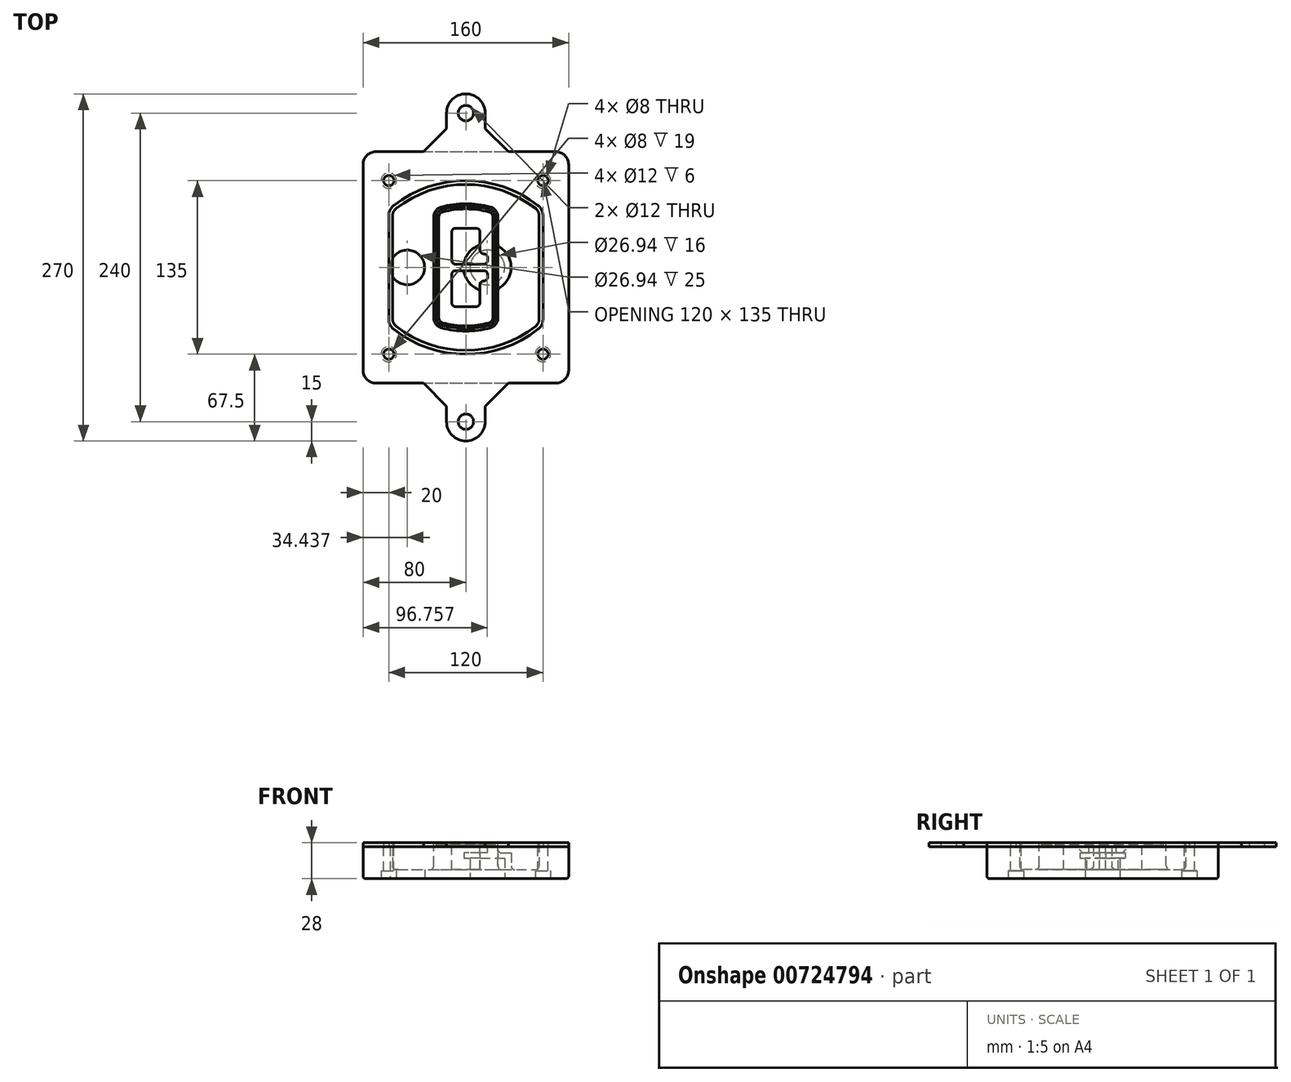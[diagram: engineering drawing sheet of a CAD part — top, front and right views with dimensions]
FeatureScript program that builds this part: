
annotation { "Feature Type Name" : "Feature", "Feature Type Description" : "" }
export const myFeature = defineFeature(function(context is Context, id is Id, definition is map)
    precondition{}
    {
        {
            var Q0;
            Q0=qCreatedBy(makeId("Top.planeOp"),FACE);
            var sketch = newSketch(context, id + "F0", { "sketchPlane" : qUnion([Q0])});
            skPoint(sketch, "E0.rect.middle", {"position": v(0, 0) * mm});
            skLineSegment(sketch, "E1.bottom", {"start": v(-70, -90) * mm, "end": v(70, -90) * mm});
            skLineSegment(sketch, "E1.top", {"start": v(-70, 90) * mm, "end": v(70, 90) * mm});
            skLineSegment(sketch, "E1.left", {"start": v(-80, -80) * mm, "end": v(-80, 80) * mm});
            skLineSegment(sketch, "E1.right", {"start": v(80, -80) * mm, "end": v(80, 80) * mm});
            skLineSegment(sketch, "E2", {"start": v(-80, 90) * mm, "end": v(80, -90) * mm, "construction": true});
            skLineSegment(sketch, "E3", {"start": v(80, 90) * mm, "end": v(-80, -90) * mm, "construction": true});
            skCircle(sketch, "E4", {"center": v(-60, 67.5) * mm, "radius": 4 * mm});
            skCircle(sketch, "E5", {"center": v(60, 67.5) * mm, "radius": 4 * mm});
            skCircle(sketch, "E6", {"center": v(60, -67.5) * mm, "radius": 4 * mm});
            skCircle(sketch, "E7", {"center": v(-60, -67.5) * mm, "radius": 4 * mm});
            skLineSegment(sketch, "E8", {"start": v(-60, 67.5) * mm, "end": v(60, 67.5) * mm, "construction": true});
            skLineSegment(sketch, "E9", {"start": v(60, 67.5) * mm, "end": v(60, -67.5) * mm, "construction": true});
            skLineSegment(sketch, "E10", {"start": v(60, -67.5) * mm, "end": v(-60, -67.5) * mm, "construction": true});
            skLineSegment(sketch, "E11", {"start": v(-60, -67.5) * mm, "end": v(-60, 67.5) * mm, "construction": true});
            skLineSegment(sketch, "E12", {"start": v(-60, 40.3) * mm, "end": v(-60, -40.3) * mm});
            skLineSegment(sketch, "E13", {"start": v(60, 40.3) * mm, "end": v(60, -40.3) * mm});
            skArc(sketch, "E14", {"start": v(56.15, 48.18) * mm, "mid": v(0, 67.5) * mm, "end": v(-56.15, 48.18) * mm});
            skArc(sketch, "E15", {"start": v(-56.15, -48.18) * mm, "mid": v(0, -67.5) * mm, "end": v(56.15, -48.18) * mm});
            skLineSegment(sketch, "E16", {"start": v(-60, 0) * mm, "end": v(60, 0) * mm, "construction": true});
            skPoint(sketch, "E17.visualSharp", {"position": v(-60, -45) * mm});
            skArc(sketch, "E17.filletArc", {"start": v(-60, -40.3) * mm, "mid": v(-58.99, -44.68) * mm, "end": v(-56.15, -48.18) * mm});
            skPoint(sketch, "E18.visualSharp", {"position": v(-60, 45) * mm});
            skArc(sketch, "E18.filletArc", {"start": v(-56.15, 48.18) * mm, "mid": v(-58.99, 44.68) * mm, "end": v(-60, 40.3) * mm});
            skPoint(sketch, "E19.visualSharp", {"position": v(60, 45) * mm});
            skArc(sketch, "E19.filletArc", {"start": v(60, 40.3) * mm, "mid": v(58.99, 44.68) * mm, "end": v(56.15, 48.18) * mm});
            skPoint(sketch, "E20.visualSharp", {"position": v(60, -45) * mm});
            skArc(sketch, "E20.filletArc", {"start": v(56.15, -48.18) * mm, "mid": v(58.99, -44.68) * mm, "end": v(60, -40.3) * mm});
            skPoint(sketch, "E21.visualSharp", {"position": v(-80, 90) * mm});
            skArc(sketch, "E21.filletArc", {"start": v(-70, 90) * mm, "mid": v(-77.07, 87.07) * mm, "end": v(-80, 80) * mm});
            skPoint(sketch, "E22.visualSharp", {"position": v(80, 90) * mm});
            skArc(sketch, "E22.filletArc", {"start": v(80, 80) * mm, "mid": v(77.07, 87.07) * mm, "end": v(70, 90) * mm});
            skPoint(sketch, "E23.visualSharp", {"position": v(80, -90) * mm});
            skArc(sketch, "E23.filletArc", {"start": v(70, -90) * mm, "mid": v(77.07, -87.07) * mm, "end": v(80, -80) * mm});
            skPoint(sketch, "E24.visualSharp", {"position": v(-80, -90) * mm});
            skArc(sketch, "E24.filletArc", {"start": v(-80, -80) * mm, "mid": v(-77.07, -87.07) * mm, "end": v(-70, -90) * mm});
            skArc(sketch, "E25.0", {"start": v(57, 40.3) * mm, "mid": v(56.3, 43.36) * mm, "end": v(54.3, 45.81) * mm});
            skLineSegment(sketch, "E25.1", {"start": v(57, 40.3) * mm, "end": v(57, -40.3) * mm});
            skArc(sketch, "E25.2", {"start": v(54.3, -45.81) * mm, "mid": v(56.3, -43.36) * mm, "end": v(57, -40.3) * mm});
            skArc(sketch, "E25.3", {"start": v(-54.3, -45.81) * mm, "mid": v(0, -64.5) * mm, "end": v(54.3, -45.81) * mm});
            skArc(sketch, "E25.4", {"start": v(-57, -40.3) * mm, "mid": v(-56.3, -43.36) * mm, "end": v(-54.3, -45.81) * mm});
            skArc(sketch, "E25.5", {"start": v(54.3, 45.81) * mm, "mid": v(0, 64.5) * mm, "end": v(-54.3, 45.81) * mm});
            skLineSegment(sketch, "E25.6", {"start": v(-57, 40.3) * mm, "end": v(-57, -40.3) * mm});
            skArc(sketch, "E25.7", {"start": v(-54.3, 45.81) * mm, "mid": v(-56.3, 43.36) * mm, "end": v(-57, 40.3) * mm});
            skArc(sketch, "E26.0", {"start": v(-58.62, 51.33) * mm, "mid": v(-62.58, 46.43) * mm, "end": v(-64, 40.3) * mm});
            skArc(sketch, "E26.1", {"start": v(58.62, 51.33) * mm, "mid": v(0, 71.5) * mm, "end": v(-58.62, 51.33) * mm});
            skArc(sketch, "E26.2", {"start": v(64, 40.3) * mm, "mid": v(62.58, 46.43) * mm, "end": v(58.62, 51.33) * mm});
            skLineSegment(sketch, "E26.3", {"start": v(64, 40.3) * mm, "end": v(64, -40.3) * mm});
            skArc(sketch, "E26.4", {"start": v(58.62, -51.33) * mm, "mid": v(62.58, -46.43) * mm, "end": v(64, -40.3) * mm});
            skLineSegment(sketch, "E26.5", {"start": v(-64, 40.3) * mm, "end": v(-64, -40.3) * mm});
            skArc(sketch, "E26.6", {"start": v(-58.62, -51.33) * mm, "mid": v(0, -71.5) * mm, "end": v(58.62, -51.33) * mm});
            skArc(sketch, "E26.7", {"start": v(-64, -40.3) * mm, "mid": v(-62.58, -46.43) * mm, "end": v(-58.62, -51.33) * mm});
            skSolve(sketch);
        }
        {
            var Q0;
            Q0=makeQuery(id+"F0.imprint","IMPRINT",FACE,{"disambiguationData":[TD([[makeQuery(id+"F0.imprint","IMPRINT",EDGE,{"derivedFrom":sQuery(id+"F0.wireOp",EDGE,"E1.bottom")}),1.0]])]});
            var Q1;
            Q1=makeQuery(id+"F0.imprint","IMPRINT",FACE,{"disambiguationData":[TD([[makeQuery(id+"F0.imprint","IMPRINT",EDGE,{"derivedFrom":sQuery(id+"F0.wireOp",EDGE,"E12")}),1.0]])]});
            var Q2;
            Q2=makeQuery(id+"F0.imprint","IMPRINT",FACE,{"disambiguationData":[TD([[makeQuery(id+"F0.imprint","IMPRINT",EDGE,{"derivedFrom":sQuery(id+"F0.wireOp",EDGE,"E25.0")}),1.0]])]});
            var Q3;
            Q3=makeQuery(id+"F0.imprint","IMPRINT",FACE,{"disambiguationData":[TD([[makeQuery(id+"F0.imprint","IMPRINT",EDGE,{"derivedFrom":sQuery(id+"F0.wireOp",EDGE,"E12")}),-1.0]])]});
            extrude(context, id + "F1", {"entities" : qUnion([Q0, Q1, Q2, Q3]), "oppositeDirection" : true, "depth" : 25 * mm});
        }
        {
            var Q0;
            Q0=makeQuery(id+"F0.imprint","IMPRINT",FACE,{"disambiguationData":[TD([[makeQuery(id+"F0.imprint","IMPRINT",EDGE,{"derivedFrom":sQuery(id+"F0.wireOp",EDGE,"E12")}),1.0]])]});
            extrude(context, id + "F2", {"entities" : qUnion([Q0]), "operationType" : NewBodyOperationType.ADD, "depth" : 3 * mm});
        }
        {
            var Q0;
            Q0=makeQuery(id+"F0.imprint","IMPRINT",FACE,{"disambiguationData":[TD([[makeQuery(id+"F0.imprint","IMPRINT",EDGE,{"derivedFrom":sQuery(id+"F0.wireOp",EDGE,"E25.0")}),1.0]])]});
            extrude(context, id + "F3", {"entities" : qUnion([Q0]), "operationType" : NewBodyOperationType.REMOVE, "oppositeDirection" : true, "depth" : 18 * mm});
        }
        {
            var Q0;
            Q0=makeQuery(id+"F2.opExtrude","CAP_FACE",FACE,{"disambiguationData":[OSD([sQuery(id+"F0.wireOp",EDGE,"E12"),sQuery(id+"F0.wireOp",EDGE,"E13"),sQuery(id+"F0.wireOp",EDGE,"E14"),sQuery(id+"F0.wireOp",EDGE,"E15"),sQuery(id+"F0.wireOp",EDGE,"E17.filletArc"),sQuery(id+"F0.wireOp",EDGE,"E18.filletArc"),sQuery(id+"F0.wireOp",EDGE,"E19.filletArc"),sQuery(id+"F0.wireOp",EDGE,"E20.filletArc"),sQuery(id+"F0.wireOp",EDGE,"E25.0"),sQuery(id+"F0.wireOp",EDGE,"E25.1"),sQuery(id+"F0.wireOp",EDGE,"E25.2"),sQuery(id+"F0.wireOp",EDGE,"E25.3"),sQuery(id+"F0.wireOp",EDGE,"E25.4"),sQuery(id+"F0.wireOp",EDGE,"E25.5"),sQuery(id+"F0.wireOp",EDGE,"E25.6"),sQuery(id+"F0.wireOp",EDGE,"E25.7")])],"isStart":false});
            var sketch = newSketch(context, id + "F4", { "sketchPlane" : qUnion([Q0])});
            skArc(sketch, "E27.0", {"start": v(-19.08, -46.97) * mm, "mid": v(0, -49.5) * mm, "end": v(19.08, -46.97) * mm});
            skArc(sketch, "E28.0", {"start": v(19.08, 46.97) * mm, "mid": v(0, 49.5) * mm, "end": v(-19.08, 46.97) * mm});
            skLineSegment(sketch, "E29", {"start": v(-25, 39.25) * mm, "end": v(-25, -39.25) * mm});
            skLineSegment(sketch, "E30", {"start": v(25, 39.25) * mm, "end": v(25, -39.25) * mm});
            skLineSegment(sketch, "E31", {"start": v(-25, 45.1) * mm, "end": v(25, 45.1) * mm, "construction": true});
            skLineSegment(sketch, "E32", {"start": v(-25, -45.1) * mm, "end": v(25, -45.1) * mm, "construction": true});
            skPoint(sketch, "E33.visualSharp", {"position": v(-25, 45.1) * mm});
            skArc(sketch, "E33.filletArc", {"start": v(-19.08, 46.97) * mm, "mid": v(-23.35, 44.11) * mm, "end": v(-25, 39.25) * mm});
            skPoint(sketch, "E34.visualSharp", {"position": v(25, 45.1) * mm});
            skArc(sketch, "E34.filletArc", {"start": v(25, 39.25) * mm, "mid": v(23.35, 44.11) * mm, "end": v(19.08, 46.97) * mm});
            skPoint(sketch, "E35.visualSharp", {"position": v(25, -45.1) * mm});
            skArc(sketch, "E35.filletArc", {"start": v(19.08, -46.97) * mm, "mid": v(23.35, -44.11) * mm, "end": v(25, -39.25) * mm});
            skPoint(sketch, "E36.visualSharp", {"position": v(-25, -45.1) * mm});
            skArc(sketch, "E36.filletArc", {"start": v(-25, -39.25) * mm, "mid": v(-23.35, -44.11) * mm, "end": v(-19.08, -46.97) * mm});
            skArc(sketch, "E37.0", {"start": v(54.3, 45.81) * mm, "mid": v(0, 64.5) * mm, "end": v(-54.3, 45.81) * mm});
            skArc(sketch, "E37.1", {"start": v(-54.3, 45.81) * mm, "mid": v(-56.3, 43.36) * mm, "end": v(-57, 40.3) * mm});
            skLineSegment(sketch, "E37.2", {"start": v(-57, 40.3) * mm, "end": v(-57, -40.3) * mm});
            skArc(sketch, "E37.3", {"start": v(-57, -40.3) * mm, "mid": v(-56.3, -43.36) * mm, "end": v(-54.3, -45.81) * mm});
            skArc(sketch, "E37.4", {"start": v(-54.3, -45.81) * mm, "mid": v(0, -64.5) * mm, "end": v(54.3, -45.81) * mm});
            skArc(sketch, "E37.5", {"start": v(54.3, -45.81) * mm, "mid": v(56.3, -43.36) * mm, "end": v(57, -40.3) * mm});
            skLineSegment(sketch, "E37.6", {"start": v(57, 40.3) * mm, "end": v(57, -40.3) * mm});
            skArc(sketch, "E37.7", {"start": v(57, 40.3) * mm, "mid": v(56.3, 43.36) * mm, "end": v(54.3, 45.81) * mm});
            skLineSegment(sketch, "E38.0", {"start": v(23, 39.25) * mm, "end": v(23, -39.25) * mm});
            skArc(sketch, "E38.1", {"start": v(18.56, -45.04) * mm, "mid": v(21.76, -42.9) * mm, "end": v(23, -39.25) * mm});
            skArc(sketch, "E38.2", {"start": v(-18.56, -45.04) * mm, "mid": v(0, -47.5) * mm, "end": v(18.56, -45.04) * mm});
            skArc(sketch, "E38.3", {"start": v(-23, -39.25) * mm, "mid": v(-21.76, -42.9) * mm, "end": v(-18.56, -45.04) * mm});
            skLineSegment(sketch, "E38.4", {"start": v(-23, 39.25) * mm, "end": v(-23, -39.25) * mm});
            skArc(sketch, "E38.5", {"start": v(23, 39.25) * mm, "mid": v(21.76, 42.9) * mm, "end": v(18.56, 45.04) * mm});
            skArc(sketch, "E38.6", {"start": v(-18.56, 45.04) * mm, "mid": v(-21.76, 42.9) * mm, "end": v(-23, 39.25) * mm});
            skArc(sketch, "E38.7", {"start": v(18.56, 45.04) * mm, "mid": v(0, 47.5) * mm, "end": v(-18.56, 45.04) * mm});
            skArc(sketch, "E39.0", {"start": v(21, 39.25) * mm, "mid": v(20.18, 41.68) * mm, "end": v(18.04, 43.1) * mm});
            skLineSegment(sketch, "E39.1", {"start": v(21, 39.25) * mm, "end": v(21, -39.25) * mm});
            skArc(sketch, "E39.2", {"start": v(18.04, -43.1) * mm, "mid": v(20.18, -41.68) * mm, "end": v(21, -39.25) * mm});
            skArc(sketch, "E39.3", {"start": v(-18.04, -43.1) * mm, "mid": v(0, -45.5) * mm, "end": v(18.04, -43.1) * mm});
            skArc(sketch, "E39.4", {"start": v(-21, -39.25) * mm, "mid": v(-20.18, -41.68) * mm, "end": v(-18.04, -43.1) * mm});
            skArc(sketch, "E39.5", {"start": v(18.04, 43.1) * mm, "mid": v(0, 45.5) * mm, "end": v(-18.04, 43.1) * mm});
            skLineSegment(sketch, "E39.6", {"start": v(-21, 39.25) * mm, "end": v(-21, -39.25) * mm});
            skArc(sketch, "E39.7", {"start": v(-18.04, 43.1) * mm, "mid": v(-20.18, 41.68) * mm, "end": v(-21, 39.25) * mm});
            skLineSegment(sketch, "E40", {"start": v(-25, 0) * mm, "end": v(25, 0) * mm, "construction": true});
            skLineSegment(sketch, "E41", {"start": v(-11, 5.5) * mm, "end": v(-11, 27.5) * mm});
            skLineSegment(sketch, "E42", {"start": v(-8, 30.5) * mm, "end": v(8, 30.5) * mm});
            skLineSegment(sketch, "E43", {"start": v(11, 27.5) * mm, "end": v(11, 13.5) * mm});
            skLineSegment(sketch, "E44", {"start": v(14, 10.5) * mm, "end": v(14, 10.5) * mm});
            skLineSegment(sketch, "E45", {"start": v(17, 7.5) * mm, "end": v(17, 5.5) * mm});
            skLineSegment(sketch, "E46", {"start": v(14, 2.5) * mm, "end": v(-8, 2.5) * mm});
            skPoint(sketch, "E47.visualSharp", {"position": v(-11, 30.5) * mm});
            skArc(sketch, "E47.filletArc", {"start": v(-8, 30.5) * mm, "mid": v(-10.12, 29.62) * mm, "end": v(-11, 27.5) * mm});
            skPoint(sketch, "E48.visualSharp", {"position": v(11, 30.5) * mm});
            skArc(sketch, "E48.filletArc", {"start": v(11, 27.5) * mm, "mid": v(10.12, 29.62) * mm, "end": v(8, 30.5) * mm});
            skPoint(sketch, "E49.visualSharp", {"position": v(11, 10.5) * mm});
            skArc(sketch, "E49.filletArc", {"start": v(11, 13.5) * mm, "mid": v(11.88, 11.38) * mm, "end": v(14, 10.5) * mm});
            skPoint(sketch, "E50.visualSharp", {"position": v(17, 10.5) * mm});
            skArc(sketch, "E50.filletArc", {"start": v(17, 7.5) * mm, "mid": v(16.12, 9.62) * mm, "end": v(14, 10.5) * mm});
            skPoint(sketch, "E51.visualSharp", {"position": v(17, 2.5) * mm});
            skArc(sketch, "E51.filletArc", {"start": v(14, 2.5) * mm, "mid": v(16.12, 3.38) * mm, "end": v(17, 5.5) * mm});
            skPoint(sketch, "E52.visualSharp", {"position": v(-11, 2.5) * mm});
            skArc(sketch, "E52.filletArc", {"start": v(-11, 5.5) * mm, "mid": v(-10.12, 3.38) * mm, "end": v(-8, 2.5) * mm});
            skLineSegment(sketch, "E53.0.MirrorCS", {"start": v(14, -2.5) * mm, "end": v(-8, -2.5) * mm});
            skArc(sketch, "E54.0.MirrorCS", {"start": v(-11, -5.5) * mm, "mid": v(-10.12, -3.38) * mm, "end": v(-8, -2.5) * mm});
            skLineSegment(sketch, "E55.0.MirrorCS", {"start": v(-11, -5.5) * mm, "end": v(-11, -27.5) * mm});
            skArc(sketch, "E56.0.MirrorCS", {"start": v(-8, -30.5) * mm, "mid": v(-10.12, -29.62) * mm, "end": v(-11, -27.5) * mm});
            skLineSegment(sketch, "E57.0.MirrorCS", {"start": v(-8, -30.5) * mm, "end": v(8, -30.5) * mm});
            skArc(sketch, "E58.0.MirrorCS", {"start": v(11, -27.5) * mm, "mid": v(10.12, -29.62) * mm, "end": v(8, -30.5) * mm});
            skLineSegment(sketch, "E59.0.MirrorCS", {"start": v(11, -27.5) * mm, "end": v(11, -13.5) * mm});
            skArc(sketch, "E60.0.MirrorCS", {"start": v(11, -13.5) * mm, "mid": v(11.88, -11.38) * mm, "end": v(14, -10.5) * mm});
            skArc(sketch, "E61.0.MirrorCS", {"start": v(17, -7.5) * mm, "mid": v(16.12, -9.62) * mm, "end": v(14, -10.5) * mm});
            skLineSegment(sketch, "E62.0.MirrorCS", {"start": v(17, -7.5) * mm, "end": v(17, -5.5) * mm});
            skArc(sketch, "E63.0.MirrorCS", {"start": v(14, -2.5) * mm, "mid": v(16.12, -3.38) * mm, "end": v(17, -5.5) * mm});
            skSolve(sketch);
        }
        {
            var Q0;
            Q0=makeQuery(id+"F4.imprint","IMPRINT",FACE,{"disambiguationData":[TD([[makeQuery(id+"F4.imprint","IMPRINT",EDGE,{"derivedFrom":sQuery(id+"F4.wireOp",EDGE,"E27.0")}),1.0]])]});
            var Q1;
            Q1=makeQuery(id+"F4.imprint","IMPRINT",FACE,{"disambiguationData":[TD([[makeQuery(id+"F4.imprint","IMPRINT",EDGE,{"derivedFrom":sQuery(id+"F4.wireOp",EDGE,"E38.0")}),-1.0]])]});
            var Q2;
            Q2=makeQuery(id+"F4.imprint","IMPRINT",FACE,{"disambiguationData":[TD([[makeQuery(id+"F4.imprint","IMPRINT",EDGE,{"derivedFrom":sQuery(id+"F4.wireOp",EDGE,"E39.0")}),1.0]])]});
            extrude(context, id + "F5", {"entities" : qUnion([Q0, Q1, Q2]), "operationType" : NewBodyOperationType.ADD, "endBound" : BoundingType.UP_TO_NEXT, "oppositeDirection" : true, "depth" : 25 * mm});
        }
        {
            var Q0;
            Q0=makeQuery(id+"F4.imprint","IMPRINT",FACE,{"disambiguationData":[TD([[makeQuery(id+"F4.imprint","IMPRINT",EDGE,{"derivedFrom":sQuery(id+"F4.wireOp",EDGE,"E38.0")}),-1.0]])]});
            extrude(context, id + "F6", {"entities" : qUnion([Q0]), "operationType" : NewBodyOperationType.REMOVE, "oppositeDirection" : true, "depth" : 2 * mm});
        }
        {
            var Q0;
            Q0=makeQuery(id+"F1.opExtrude","CAP_FACE",FACE,{"disambiguationData":[OSD([sQuery(id+"F0.wireOp",EDGE,"E1.bottom"),sQuery(id+"F0.wireOp",EDGE,"E1.top"),sQuery(id+"F0.wireOp",EDGE,"E1.left"),sQuery(id+"F0.wireOp",EDGE,"E1.right"),sQuery(id+"F0.wireOp",EDGE,"E4"),sQuery(id+"F0.wireOp",EDGE,"E5"),sQuery(id+"F0.wireOp",EDGE,"E6"),sQuery(id+"F0.wireOp",EDGE,"E7"),sQuery(id+"F0.wireOp",EDGE,"E21.filletArc"),sQuery(id+"F0.wireOp",EDGE,"E22.filletArc"),sQuery(id+"F0.wireOp",EDGE,"E23.filletArc"),sQuery(id+"F0.wireOp",EDGE,"E24.filletArc")])],"isStart":false});
            var sketch = newSketch(context, id + "F7", { "sketchPlane" : qUnion([Q0])});
            skCircle(sketch, "E64", {"center": v(16.76, 0) * mm, "radius": 13.47 * mm});
            skCircle(sketch, "E65", {"center": v(-45.56, 0) * mm, "radius": 13.47 * mm});
            skLineSegment(sketch, "E66", {"start": v(80, 0) * mm, "end": v(-80, 0) * mm});
            skCircle(sketch, "E67", {"center": v(16.76, 0) * mm, "radius": 18.47 * mm});
            skCircle(sketch, "E68", {"center": v(60, -67.5) * mm, "radius": 6 * mm});
            skCircle(sketch, "E69", {"center": v(-60, -67.5) * mm, "radius": 6 * mm});
            skCircle(sketch, "E70", {"center": v(-60, 67.5) * mm, "radius": 6 * mm});
            skCircle(sketch, "E71", {"center": v(60, 67.5) * mm, "radius": 6 * mm});
            skSolve(sketch);
        }
        {
            var Q0;
            {var subQ1=sQuery(id+"F7.wireOp",EDGE,"E66");var subQ4=sQuery(id+"F7.wireOp",EDGE,"E64");var subQ6=makeQuery(id+"F7.imprint","INTERSECT",VERTEX,{"disambiguationData":[OD(0.0)],"derivedFrom":[subQ4,subQ1]});Q0=makeQuery(id+"F7.imprint","IMPRINT",FACE,{"disambiguationData":[TD([[makeQuery(id+"F7.imprint","IMPRINT",EDGE,{"disambiguationData":[TD([[subQ6,-1.0]])],"derivedFrom":subQ4}),-1.0]])]});}
            var Q1;
            {var subQ0=sQuery(id+"F7.wireOp",EDGE,"E66");var subQ1=sQuery(id+"F7.wireOp",EDGE,"E64");var subQ3=makeQuery(id+"F7.imprint","INTERSECT",VERTEX,{"disambiguationData":[OD(0.0)],"derivedFrom":[subQ1,subQ0]});Q1=makeQuery(id+"F7.imprint","IMPRINT",FACE,{"disambiguationData":[TD([[makeQuery(id+"F7.imprint","IMPRINT",EDGE,{"disambiguationData":[TD([[subQ3,-1.0]])],"derivedFrom":subQ1}),1.0]])]});}
            var Q2;
            {var subQ0=sQuery(id+"F7.wireOp",EDGE,"E66");var subQ1=sQuery(id+"F7.wireOp",EDGE,"E64");var subQ3=makeQuery(id+"F7.imprint","INTERSECT",VERTEX,{"disambiguationData":[OD(0.0)],"derivedFrom":[subQ1,subQ0]});Q2=makeQuery(id+"F7.imprint","IMPRINT",FACE,{"disambiguationData":[TD([[makeQuery(id+"F7.imprint","IMPRINT",EDGE,{"disambiguationData":[TD([[subQ3,1.0]])],"derivedFrom":subQ1}),1.0]])]});}
            var Q3;
            {var subQ1=sQuery(id+"F7.wireOp",EDGE,"E66");var subQ4=sQuery(id+"F7.wireOp",EDGE,"E64");var subQ6=makeQuery(id+"F7.imprint","INTERSECT",VERTEX,{"disambiguationData":[OD(0.0)],"derivedFrom":[subQ4,subQ1]});Q3=makeQuery(id+"F7.imprint","IMPRINT",FACE,{"disambiguationData":[TD([[makeQuery(id+"F7.imprint","IMPRINT",EDGE,{"disambiguationData":[TD([[subQ6,1.0]])],"derivedFrom":subQ4}),-1.0]])]});}
            extrude(context, id + "F8", {"entities" : qUnion([Q0, Q1, Q2, Q3]), "operationType" : NewBodyOperationType.ADD, "oppositeDirection" : true, "depth" : 20 * mm});
        }
        {
            var Q0;
            {var subQ0=sQuery(id+"F7.wireOp",EDGE,"E66");var subQ1=sQuery(id+"F7.wireOp",EDGE,"E64");var subQ3=makeQuery(id+"F7.imprint","INTERSECT",VERTEX,{"disambiguationData":[OD(0.0)],"derivedFrom":[subQ1,subQ0]});Q0=makeQuery(id+"F7.imprint","IMPRINT",FACE,{"disambiguationData":[TD([[makeQuery(id+"F7.imprint","IMPRINT",EDGE,{"disambiguationData":[TD([[subQ3,-1.0]])],"derivedFrom":subQ1}),1.0]])]});}
            var Q1;
            {var subQ0=sQuery(id+"F7.wireOp",EDGE,"E66");var subQ1=sQuery(id+"F7.wireOp",EDGE,"E64");var subQ3=makeQuery(id+"F7.imprint","INTERSECT",VERTEX,{"disambiguationData":[OD(0.0)],"derivedFrom":[subQ1,subQ0]});Q1=makeQuery(id+"F7.imprint","IMPRINT",FACE,{"disambiguationData":[TD([[makeQuery(id+"F7.imprint","IMPRINT",EDGE,{"disambiguationData":[TD([[subQ3,1.0]])],"derivedFrom":subQ1}),1.0]])]});}
            extrude(context, id + "F9", {"entities" : qUnion([Q0, Q1]), "operationType" : NewBodyOperationType.REMOVE, "oppositeDirection" : true, "depth" : 16 * mm});
        }
        {
            var Q0;
            {var subQ0=sQuery(id+"F7.wireOp",EDGE,"E66");var subQ1=sQuery(id+"F7.wireOp",EDGE,"E65");var subQ3=makeQuery(id+"F7.imprint","INTERSECT",VERTEX,{"disambiguationData":[OD(0.0)],"derivedFrom":[subQ1,subQ0]});Q0=makeQuery(id+"F7.imprint","IMPRINT",FACE,{"disambiguationData":[TD([[makeQuery(id+"F7.imprint","IMPRINT",EDGE,{"disambiguationData":[TD([[subQ3,-1.0]])],"derivedFrom":subQ1}),1.0]])]});}
            var Q1;
            {var subQ0=sQuery(id+"F7.wireOp",EDGE,"E66");var subQ1=sQuery(id+"F7.wireOp",EDGE,"E65");var subQ3=makeQuery(id+"F7.imprint","INTERSECT",VERTEX,{"disambiguationData":[OD(0.0)],"derivedFrom":[subQ1,subQ0]});Q1=makeQuery(id+"F7.imprint","IMPRINT",FACE,{"disambiguationData":[TD([[makeQuery(id+"F7.imprint","IMPRINT",EDGE,{"disambiguationData":[TD([[subQ3,1.0]])],"derivedFrom":subQ1}),1.0]])]});}
            extrude(context, id + "F10", {"entities" : qUnion([Q0, Q1]), "operationType" : NewBodyOperationType.REMOVE, "oppositeDirection" : true, "depth" : 25 * mm});
        }
        {
            var Q0;
            Q0=makeQuery(id+"F7.imprint","IMPRINT",FACE,{"disambiguationData":[TD([[makeQuery(id+"F7.imprint","IMPRINT",EDGE,{"derivedFrom":sQuery(id+"F7.wireOp",EDGE,"E68")}),1.0]])]});
            var Q1;
            Q1=makeQuery(id+"F7.imprint","IMPRINT",FACE,{"disambiguationData":[TD([[makeQuery(id+"F7.imprint","IMPRINT",EDGE,{"derivedFrom":makeQuery(id+"F1.opExtrude","CAP_EDGE",EDGE,{"disambiguationData":[OSD([sQuery(id+"F0.wireOp",EDGE,"E5")])],"isStart":false})}),-1.0]])]});
            var Q2;
            Q2=makeQuery(id+"F7.imprint","IMPRINT",FACE,{"disambiguationData":[TD([[makeQuery(id+"F7.imprint","IMPRINT",EDGE,{"derivedFrom":sQuery(id+"F7.wireOp",EDGE,"E69")}),1.0]])]});
            var Q3;
            Q3=makeQuery(id+"F7.imprint","IMPRINT",FACE,{"disambiguationData":[TD([[makeQuery(id+"F7.imprint","IMPRINT",EDGE,{"derivedFrom":makeQuery(id+"F1.opExtrude","CAP_EDGE",EDGE,{"disambiguationData":[OSD([sQuery(id+"F0.wireOp",EDGE,"E4")])],"isStart":false})}),-1.0]])]});
            var Q4;
            Q4=makeQuery(id+"F7.imprint","IMPRINT",FACE,{"disambiguationData":[TD([[makeQuery(id+"F7.imprint","IMPRINT",EDGE,{"derivedFrom":sQuery(id+"F7.wireOp",EDGE,"E70")}),1.0]])]});
            var Q5;
            Q5=makeQuery(id+"F7.imprint","IMPRINT",FACE,{"disambiguationData":[TD([[makeQuery(id+"F7.imprint","IMPRINT",EDGE,{"derivedFrom":makeQuery(id+"F1.opExtrude","CAP_EDGE",EDGE,{"disambiguationData":[OSD([sQuery(id+"F0.wireOp",EDGE,"E7")])],"isStart":false})}),-1.0]])]});
            var Q6;
            Q6=makeQuery(id+"F7.imprint","IMPRINT",FACE,{"disambiguationData":[TD([[makeQuery(id+"F7.imprint","IMPRINT",EDGE,{"derivedFrom":sQuery(id+"F7.wireOp",EDGE,"E71")}),1.0]])]});
            var Q7;
            Q7=makeQuery(id+"F7.imprint","IMPRINT",FACE,{"disambiguationData":[TD([[makeQuery(id+"F7.imprint","IMPRINT",EDGE,{"derivedFrom":makeQuery(id+"F1.opExtrude","CAP_EDGE",EDGE,{"disambiguationData":[OSD([sQuery(id+"F0.wireOp",EDGE,"E6")])],"isStart":false})}),-1.0]])]});
            extrude(context, id + "F11", {"entities" : qUnion([Q0, Q1, Q2, Q3, Q4, Q5, Q6, Q7]), "operationType" : NewBodyOperationType.REMOVE, "oppositeDirection" : true, "depth" : 6 * mm});
        }
        {
            var Q0;
            Q0=makeQuery(id+"F9.boolean.opBoolean","COPY",FACE,{"derivedFrom":makeQuery(id+"F9.opExtrude","CAP_FACE",FACE,{"disambiguationData":[OSD([sQuery(id+"F7.wireOp",EDGE,"E64")])],"isStart":false})});
            var sketch = newSketch(context, id + "F12", { "sketchPlane" : qUnion([Q0])});
            skArc(sketch, "E72.0", {"start": v(11, 17.55) * mm, "mid": v(2.57, 11.82) * mm, "end": v(-1.54, 2.5) * mm});
            skArc(sketch, "E72.1", {"start": v(-1.54, -2.5) * mm, "mid": v(2.57, -11.82) * mm, "end": v(11, -17.55) * mm});
            skLineSegment(sketch, "E73", {"start": v(-1.54, -2.5) * mm, "end": v(14, -2.5) * mm});
            skLineSegment(sketch, "E74.0", {"start": v(14, 2.5) * mm, "end": v(-1.54, 2.5) * mm});
            skArc(sketch, "E74.1", {"start": v(14, 2.5) * mm, "mid": v(16.12, 3.38) * mm, "end": v(17, 5.5) * mm});
            skLineSegment(sketch, "E74.2", {"start": v(17, 7.5) * mm, "end": v(17, 5.5) * mm});
            skArc(sketch, "E74.3", {"start": v(17, 7.5) * mm, "mid": v(16.12, 9.62) * mm, "end": v(14, 10.5) * mm});
            skArc(sketch, "E74.4", {"start": v(11, 13.5) * mm, "mid": v(11.88, 11.38) * mm, "end": v(14, 10.5) * mm});
            skLineSegment(sketch, "E74.5", {"start": v(11, 17.55) * mm, "end": v(11, 13.5) * mm});
            skLineSegment(sketch, "E74.7", {"start": v(14, -2.5) * mm, "end": v(-1.54, -2.5) * mm});
            skArc(sketch, "E74.8", {"start": v(14, -2.5) * mm, "mid": v(16.12, -3.38) * mm, "end": v(17, -5.5) * mm});
            skLineSegment(sketch, "E74.9", {"start": v(17, -7.5) * mm, "end": v(17, -5.5) * mm});
            skArc(sketch, "E74.10", {"start": v(17, -7.5) * mm, "mid": v(16.12, -9.62) * mm, "end": v(14, -10.5) * mm});
            skArc(sketch, "E74.11", {"start": v(11, -13.5) * mm, "mid": v(11.88, -11.38) * mm, "end": v(14, -10.5) * mm});
            skLineSegment(sketch, "E74.12", {"start": v(11, -17.55) * mm, "end": v(11, -13.5) * mm});
            skPoint(sketch, "E75.orphan", {"position": v(11, -27.5) * mm});
            skPoint(sketch, "E76.orphan", {"position": v(-8, -2.5) * mm});
            skPoint(sketch, "E77.orphan", {"position": v(-8, 2.5) * mm});
            skPoint(sketch, "E78.orphan", {"position": v(11, 27.5) * mm});
            skSolve(sketch);
        }
        {
            var Q0;
            {var subQ7=sQuery(id+"F12.wireOp",EDGE,"E72.0");var subQ14=sQuery(id+"F12.wireOp",EDGE,"E72.1");var subQ16=sQuery(id+"F12.wireOp",EDGE,"E74.1");var subQ18=sQuery(id+"F12.wireOp",EDGE,"E74.8");Q0=qUnion([makeQuery(id+"F12.imprint","IMPRINT",FACE,{"disambiguationData":[TD([[makeQuery(id+"F12.imprint","IMPRINT",EDGE,{"derivedFrom":subQ7}),1.0]])]}),makeQuery(id+"F12.imprint","IMPRINT",FACE,{"disambiguationData":[TD([[makeQuery(id+"F12.imprint","IMPRINT",EDGE,{"derivedFrom":subQ14}),1.0]])]}),makeQuery(id+"F12.imprint","IMPRINT",FACE,{"disambiguationData":[TD([[makeQuery(id+"F12.imprint","IMPRINT",EDGE,{"derivedFrom":subQ16}),1.0]])]}),makeQuery(id+"F12.imprint","IMPRINT",FACE,{"disambiguationData":[TD([[makeQuery(id+"F12.imprint","IMPRINT",EDGE,{"derivedFrom":subQ18}),-1.0]])]})]);}
            var Q1;
            Q1=makeQuery(id+"F5.boolean.opBoolean","SPLIT",FACE,{"disambiguationData":[TD([makeQuery(id+"F5.opExtrude","SWEPT_FACE",FACE,{"disambiguationData":[OSD([sQuery(id+"F4.wireOp",EDGE,"E41")])]})])],"derivedFrom":makeQuery(id+"F3.boolean.opBoolean","COPY",FACE,{"derivedFrom":makeQuery(id+"F3.opExtrude","CAP_FACE",FACE,{"disambiguationData":[OSD([sQuery(id+"F0.wireOp",EDGE,"E25.0"),sQuery(id+"F0.wireOp",EDGE,"E25.1"),sQuery(id+"F0.wireOp",EDGE,"E25.2"),sQuery(id+"F0.wireOp",EDGE,"E25.3"),sQuery(id+"F0.wireOp",EDGE,"E25.4"),sQuery(id+"F0.wireOp",EDGE,"E25.5"),sQuery(id+"F0.wireOp",EDGE,"E25.6"),sQuery(id+"F0.wireOp",EDGE,"E25.7")])],"isStart":false})})});
            extrude(context, id + "F13", {"entities" : qUnion([Q0]), "operationType" : NewBodyOperationType.REMOVE, "endBound" : BoundingType.UP_TO_SURFACE, "endBoundEntityFace" : qUnion([Q1]), "depth" : 25 * mm});
        }
        {
            var Q0;
            Q0=makeQuery(id+"F3.boolean.opBoolean","COPY",EDGE,{"derivedFrom":makeQuery(id+"F3.opExtrude","CAP_EDGE",EDGE,{"disambiguationData":[OSD([sQuery(id+"F0.wireOp",EDGE,"E25.6")])],"isStart":false})});
            var Q1;
            Q1=makeQuery(id+"F8.boolean.opBoolean","INTERSECT",EDGE,{"derivedFrom":[makeQuery(id+"F5.opExtrude","SWEPT_FACE",FACE,{"disambiguationData":[OSD([sQuery(id+"F4.wireOp",EDGE,"E30")])]}),makeQuery(id+"F8.opExtrude","CAP_FACE",FACE,{"disambiguationData":[OSD([sQuery(id+"F7.wireOp",EDGE,"E67")])],"isStart":false})]});
            var Q2;
            Q2=makeQuery(id+"F8.boolean.opBoolean","INTERSECT",EDGE,{"disambiguationData":[OD(1.0)],"derivedFrom":[makeQuery(id+"F5.opExtrude","SWEPT_FACE",FACE,{"disambiguationData":[OSD([sQuery(id+"F4.wireOp",EDGE,"E30")])]}),makeQuery(id+"F8.opExtrude","SWEPT_FACE",FACE,{"disambiguationData":[OSD([sQuery(id+"F7.wireOp",EDGE,"E67")])]})]});
            var Q3;
            {var subQ0=sQuery(id+"F4.wireOp",EDGE,"E30");Q3=makeQuery(id+"F8.boolean.opBoolean","SPLIT",EDGE,{"disambiguationData":[TD([makeQuery(id+"F5.opExtrude","SWEPT_FACE",FACE,{"disambiguationData":[OSD([sQuery(id+"F4.wireOp",EDGE,"E35.filletArc")])]})])],"derivedFrom":makeQuery(id+"F5.opExtrude","CAP_EDGE",EDGE,{"disambiguationData":[OSD([subQ0])],"isStart":false})});}
            var Q4;
            {var subQ0=sQuery(id+"F0.wireOp",EDGE,"E25.7");var subQ1=sQuery(id+"F0.wireOp",EDGE,"E25.1");var subQ2=sQuery(id+"F0.wireOp",EDGE,"E25.6");var subQ3=sQuery(id+"F0.wireOp",EDGE,"E25.5");var subQ4=sQuery(id+"F0.wireOp",EDGE,"E25.4");var subQ5=sQuery(id+"F0.wireOp",EDGE,"E25.0");var subQ6=sQuery(id+"F0.wireOp",EDGE,"E25.2");var subQ7=sQuery(id+"F0.wireOp",EDGE,"E25.3");Q4=makeQuery(id+"F8.boolean.opBoolean","INTERSECT",EDGE,{"derivedFrom":[makeQuery(id+"F5.boolean.opBoolean","SPLIT",FACE,{"disambiguationData":[TD([makeQuery(id+"F2.opExtrude","SWEPT_FACE",FACE,{"disambiguationData":[OSD([subQ5])]})])],"derivedFrom":makeQuery(id+"F3.boolean.opBoolean","COPY",FACE,{"derivedFrom":makeQuery(id+"F3.opExtrude","CAP_FACE",FACE,{"disambiguationData":[OSD([subQ5,subQ1,subQ6,subQ7,subQ4,subQ3,subQ2,subQ0])],"isStart":false})})}),makeQuery(id+"F8.opExtrude","SWEPT_FACE",FACE,{"disambiguationData":[OSD([sQuery(id+"F7.wireOp",EDGE,"E67")])]})]});}
            var Q5;
            Q5=makeQuery(id+"F8.boolean.opBoolean","INTERSECT",EDGE,{"disambiguationData":[OD(0.0)],"derivedFrom":[makeQuery(id+"F5.opExtrude","SWEPT_FACE",FACE,{"disambiguationData":[OSD([sQuery(id+"F4.wireOp",EDGE,"E30")])]}),makeQuery(id+"F8.opExtrude","SWEPT_FACE",FACE,{"disambiguationData":[OSD([sQuery(id+"F7.wireOp",EDGE,"E67")])]})]});
            fillet(context, id + "F14", {"entities" : qUnion([Q0, Q1, Q2, Q3, Q4, Q5]), "radius" : 3 * mm, "tangentPropagation" : true, "allowEdgeOverflow" : false});
        }
        {
            var Q0;
            Q0=makeQuery(id+"F1.opExtrude","CAP_EDGE",EDGE,{"disambiguationData":[OSD([sQuery(id+"F0.wireOp",EDGE,"E1.bottom")])],"isStart":false});
            fillet(context, id + "F15", {"entities" : qUnion([Q0]), "radius" : 2 * mm, "tangentPropagation" : true, "allowEdgeOverflow" : false});
        }
        {
            var Q0;
            {var subQ0=sQuery(id+"F0.wireOp",EDGE,"E21.filletArc");var subQ1=sQuery(id+"F0.wireOp",EDGE,"E7");var subQ2=sQuery(id+"F0.wireOp",EDGE,"E6");var subQ3=sQuery(id+"F0.wireOp",EDGE,"E5");var subQ4=sQuery(id+"F0.wireOp",EDGE,"E4");var subQ5=sQuery(id+"F0.wireOp",EDGE,"E22.filletArc");var subQ6=sQuery(id+"F0.wireOp",EDGE,"E1.bottom");var subQ7=sQuery(id+"F0.wireOp",EDGE,"E1.right");var subQ8=sQuery(id+"F0.wireOp",EDGE,"E1.top");var subQ9=sQuery(id+"F0.wireOp",EDGE,"E1.left");var subQ10=sQuery(id+"F0.wireOp",EDGE,"E23.filletArc");var subQ11=sQuery(id+"F0.wireOp",EDGE,"E24.filletArc");Q0=makeQuery(id+"F2.boolean.opBoolean","SPLIT",FACE,{"disambiguationData":[TD([makeQuery(id+"F1.opExtrude","SWEPT_FACE",FACE,{"disambiguationData":[OSD([subQ6])]})])],"derivedFrom":makeQuery(id+"F1.opExtrude","CAP_FACE",FACE,{"disambiguationData":[OSD([subQ6,subQ8,subQ9,subQ7,subQ4,subQ3,subQ2,subQ1,subQ0,subQ5,subQ10,subQ11])],"isStart":true})});}
            var sketch = newSketch(context, id + "F16", { "sketchPlane" : qUnion([Q0])});
            skLineSegment(sketch, "E79", {"start": v(-80, 0) * mm, "end": v(80, 0) * mm, "construction": true});
            skPoint(sketch, "E80.start.orphan", {"position": v(0, 90) * mm});
            skLineSegment(sketch, "E81", {"start": v(0, 90) * mm, "end": v(0, 120) * mm, "construction": true});
            skCircle(sketch, "E82", {"center": v(0, 120) * mm, "radius": 6 * mm});
            skLineSegment(sketch, "E83", {"start": v(-33, 90) * mm, "end": v(-15, 108) * mm});
            skLineSegment(sketch, "E84", {"start": v(-15, 108) * mm, "end": v(-15, 120) * mm});
            skLineSegment(sketch, "E85.MirrorCS", {"start": v(15, 108) * mm, "end": v(15, 120) * mm});
            skLineSegment(sketch, "E86.MirrorCS", {"start": v(33, 90) * mm, "end": v(15, 108) * mm});
            skArc(sketch, "E87", {"start": v(15, 120) * mm, "mid": v(0, 135) * mm, "end": v(-15, 120) * mm});
            skLineSegment(sketch, "E88.MirrorCS", {"start": v(-33, -90) * mm, "end": v(-15, -108) * mm});
            skLineSegment(sketch, "E89.MirrorCS", {"start": v(0, -90) * mm, "end": v(0, -120) * mm, "construction": true});
            skLineSegment(sketch, "E90.MirrorCS", {"start": v(33, -90) * mm, "end": v(15, -108) * mm});
            skLineSegment(sketch, "E91.MirrorCS", {"start": v(15, -108) * mm, "end": v(15, -120) * mm});
            skCircle(sketch, "E92.MirrorC", {"center": v(0, -120) * mm, "radius": 6 * mm});
            skArc(sketch, "E93.MirrorCS", {"start": v(15, -120) * mm, "mid": v(0, -135) * mm, "end": v(-15, -120) * mm});
            skLineSegment(sketch, "E94.MirrorCS", {"start": v(-15, -108) * mm, "end": v(-15, -120) * mm});
            skSolve(sketch);
        }
        {
            var Q0;
            Q0=makeQuery(id+"F16.imprint","IMPRINT",FACE,{"disambiguationData":[TD([[makeQuery(id+"F16.imprint","IMPRINT",EDGE,{"derivedFrom":makeQuery(id+"F1.opExtrude","CAP_EDGE",EDGE,{"disambiguationData":[OSD([sQuery(id+"F0.wireOp",EDGE,"E1.left")])],"isStart":true})}),-1.0]])]});
            var Q1;
            Q1=makeQuery(id+"F16.imprint","IMPRINT",FACE,{"disambiguationData":[TD([[makeQuery(id+"F16.imprint","IMPRINT",EDGE,{"derivedFrom":sQuery(id+"F16.wireOp",EDGE,"E82")}),-1.0]])]});
            var Q2;
            {var subQ1=sQuery(id+"F16.wireOp",EDGE,"E88.MirrorCS");Q2=makeQuery(id+"F16.imprint","IMPRINT",FACE,{"disambiguationData":[TD([[makeQuery(id+"F16.imprint","IMPRINT",EDGE,{"derivedFrom":subQ1}),1.0]])]});}
            var Q3;
            Q3=makeQuery(id+"F2.opExtrude","CAP_FACE",FACE,{"disambiguationData":[OSD([sQuery(id+"F0.wireOp",EDGE,"E12"),sQuery(id+"F0.wireOp",EDGE,"E13"),sQuery(id+"F0.wireOp",EDGE,"E14"),sQuery(id+"F0.wireOp",EDGE,"E15"),sQuery(id+"F0.wireOp",EDGE,"E17.filletArc"),sQuery(id+"F0.wireOp",EDGE,"E18.filletArc"),sQuery(id+"F0.wireOp",EDGE,"E19.filletArc"),sQuery(id+"F0.wireOp",EDGE,"E20.filletArc"),sQuery(id+"F0.wireOp",EDGE,"E25.0"),sQuery(id+"F0.wireOp",EDGE,"E25.1"),sQuery(id+"F0.wireOp",EDGE,"E25.2"),sQuery(id+"F0.wireOp",EDGE,"E25.3"),sQuery(id+"F0.wireOp",EDGE,"E25.4"),sQuery(id+"F0.wireOp",EDGE,"E25.5"),sQuery(id+"F0.wireOp",EDGE,"E25.6"),sQuery(id+"F0.wireOp",EDGE,"E25.7")])],"isStart":false});
            extrude(context, id + "F17", {"entities" : qUnion([Q0, Q1, Q2]), "endBound" : BoundingType.UP_TO_SURFACE, "depth" : 25 * mm, "endBoundEntityFace" : qUnion([Q3]), "offsetDistance" : 25 * mm});
        }
    });
